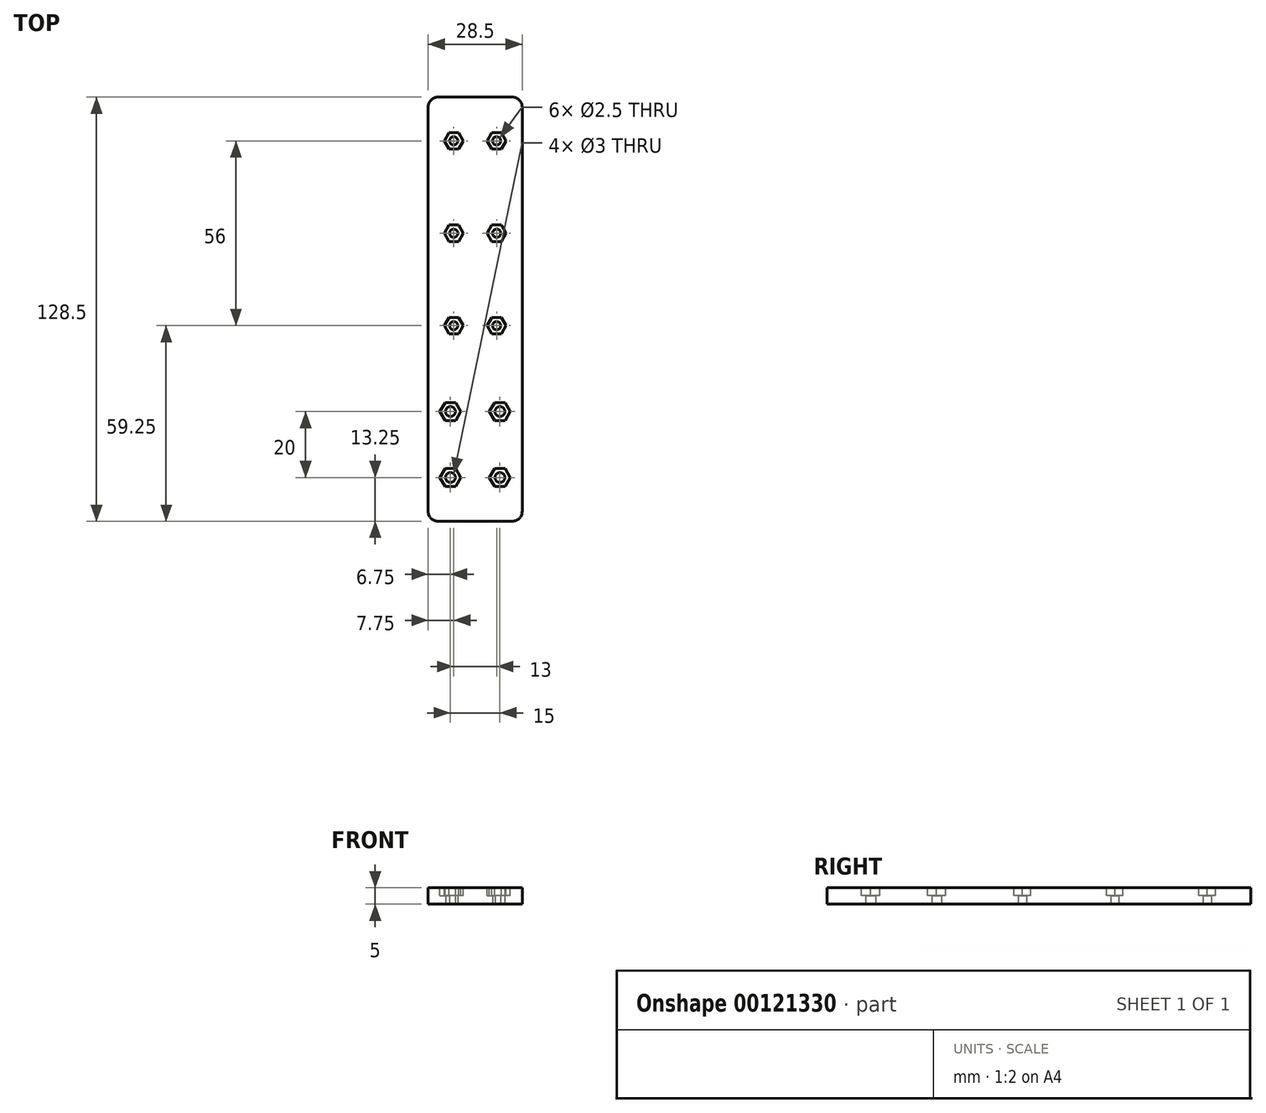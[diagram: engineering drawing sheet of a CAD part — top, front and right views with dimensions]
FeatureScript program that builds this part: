
annotation { "Feature Type Name" : "Feature", "Feature Type Description" : "" }
export const myFeature = defineFeature(function(context is Context, id is Id, definition is map)
    precondition{}
    {
        {
            var Q0;
            Q0=qCreatedBy(makeId("Top.planeOp"),FACE);
            var sketch = newSketch(context, id + "F0", { "sketchPlane" : qUnion([Q0])});
            skCircle(sketch, "E0", {"center": v(7.75, 59.25) * mm, "radius": 1.25 * mm});
            skCircle(sketch, "E1.0.1.0", {"center": v(7.75, 87.25) * mm, "radius": 1.25 * mm});
            skCircle(sketch, "E1.0.2.0", {"center": v(7.75, 115.25) * mm, "radius": 1.25 * mm});
            skCircle(sketch, "E1.1.0.0", {"center": v(20.75, 59.25) * mm, "radius": 1.25 * mm});
            skCircle(sketch, "E1.1.1.0", {"center": v(20.75, 87.25) * mm, "radius": 1.25 * mm});
            skCircle(sketch, "E1.1.2.0", {"center": v(20.75, 115.25) * mm, "radius": 1.25 * mm});
            skLineSegment(sketch, "E1.direction1", {"start": v(7.75, 59.25) * mm, "end": v(20.75, 59.25) * mm, "construction": true});
            skLineSegment(sketch, "E1.direction2", {"start": v(7.75, 59.25) * mm, "end": v(7.75, 87.25) * mm, "construction": true});
            skLineSegment(sketch, "E2.bottom", {"start": v(0, 0) * mm, "end": v(28.5, 0) * mm});
            skLineSegment(sketch, "E2.top", {"start": v(0, 128.5) * mm, "end": v(28.5, 128.5) * mm});
            skLineSegment(sketch, "E2.left", {"start": v(0, 0) * mm, "end": v(0, 128.5) * mm});
            skLineSegment(sketch, "E2.right", {"start": v(28.5, 0) * mm, "end": v(28.5, 128.5) * mm});
            skCircle(sketch, "E3", {"center": v(6.75, 13.25) * mm, "radius": 1.5 * mm});
            skCircle(sketch, "E4.0.1.0", {"center": v(6.75, 33.25) * mm, "radius": 1.5 * mm});
            skCircle(sketch, "E4.1.0.0", {"center": v(21.75, 13.25) * mm, "radius": 1.5 * mm});
            skCircle(sketch, "E4.1.1.0", {"center": v(21.75, 33.25) * mm, "radius": 1.5 * mm});
            skLineSegment(sketch, "E4.direction1", {"start": v(6.75, 13.25) * mm, "end": v(21.75, 13.25) * mm, "construction": true});
            skLineSegment(sketch, "E4.direction2", {"start": v(6.75, 13.25) * mm, "end": v(6.75, 33.25) * mm, "construction": true});
            skPoint(sketch, "E5", {"position": v(14.25, 59.25) * mm});
            skPoint(sketch, "E6", {"position": v(14.25, 13.25) * mm});
            skSolve(sketch);
        }
        {
            var Q0;
            Q0=makeQuery(id+"F0.imprint","IMPRINT",FACE,{"disambiguationData":[TD([[makeQuery(id+"F0.imprint","IMPRINT",EDGE,{"derivedFrom":sQuery(id+"F0.wireOp",EDGE,"E0")}),-1.0]])]});
            extrude(context, id + "F1", {"entities" : qUnion([Q0]), "depth" : 5 * mm});
        }
        {
            var Q0;
            Q0=makeQuery(id+"F1.opExtrude","CAP_FACE",FACE,{"disambiguationData":[OSD([sQuery(id+"F0.wireOp",EDGE,"E0"),sQuery(id+"F0.wireOp",EDGE,"E1.0.1.0"),sQuery(id+"F0.wireOp",EDGE,"E1.0.2.0"),sQuery(id+"F0.wireOp",EDGE,"E1.1.0.0"),sQuery(id+"F0.wireOp",EDGE,"E1.1.1.0"),sQuery(id+"F0.wireOp",EDGE,"E1.1.2.0"),sQuery(id+"F0.wireOp",EDGE,"E2.bottom"),sQuery(id+"F0.wireOp",EDGE,"E2.top"),sQuery(id+"F0.wireOp",EDGE,"E2.left"),sQuery(id+"F0.wireOp",EDGE,"E2.right"),sQuery(id+"F0.wireOp",EDGE,"E3"),sQuery(id+"F0.wireOp",EDGE,"E4.0.1.0"),sQuery(id+"F0.wireOp",EDGE,"E4.1.0.0"),sQuery(id+"F0.wireOp",EDGE,"E4.1.1.0")])],"isStart":false});
            var sketch = newSketch(context, id + "F2", { "sketchPlane" : qUnion([Q0])});
            skCircle(sketch, "E7.cCircle", {"center": v(21.75, 13.25) * mm, "radius": 2.75 * mm, "construction": true});
            skLineSegment(sketch, "E7.0", {"start": v(23.34, 10.5) * mm, "end": v(20.16, 10.5) * mm});
            skLineSegment(sketch, "E7.1", {"start": v(20.16, 10.5) * mm, "end": v(18.57, 13.25) * mm});
            skLineSegment(sketch, "E7.2", {"start": v(18.57, 13.25) * mm, "end": v(20.16, 16) * mm});
            skLineSegment(sketch, "E7.3", {"start": v(20.16, 16) * mm, "end": v(23.34, 16) * mm});
            skLineSegment(sketch, "E7.4", {"start": v(23.34, 16) * mm, "end": v(24.93, 13.25) * mm});
            skLineSegment(sketch, "E7.5", {"start": v(24.93, 13.25) * mm, "end": v(23.34, 10.5) * mm});
            skPoint(sketch, "E7.0.midPoint", {"position": v(21.75, 10.5) * mm});
            skCircle(sketch, "E8.cCircle", {"center": v(7.75, 59.25) * mm, "radius": 2.5 * mm, "construction": true});
            skLineSegment(sketch, "E8.0", {"start": v(9.2, 56.75) * mm, "end": v(6.3, 56.75) * mm});
            skLineSegment(sketch, "E8.1", {"start": v(6.3, 56.75) * mm, "end": v(4.86, 59.25) * mm});
            skLineSegment(sketch, "E8.2", {"start": v(4.86, 59.25) * mm, "end": v(6.3, 61.75) * mm});
            skLineSegment(sketch, "E8.3", {"start": v(6.3, 61.75) * mm, "end": v(9.2, 61.75) * mm});
            skLineSegment(sketch, "E8.4", {"start": v(9.2, 61.75) * mm, "end": v(10.64, 59.25) * mm});
            skLineSegment(sketch, "E8.5", {"start": v(10.64, 59.25) * mm, "end": v(9.2, 56.75) * mm});
            skPoint(sketch, "E8.0.midPoint", {"position": v(7.75, 56.75) * mm});
            skCircle(sketch, "E9.cCircle", {"center": v(6.75, 33.25) * mm, "radius": 2.75 * mm, "construction": true});
            skLineSegment(sketch, "E9.0", {"start": v(8.34, 30.5) * mm, "end": v(5.16, 30.5) * mm});
            skLineSegment(sketch, "E9.1", {"start": v(5.16, 30.5) * mm, "end": v(3.57, 33.25) * mm});
            skLineSegment(sketch, "E9.2", {"start": v(3.57, 33.25) * mm, "end": v(5.16, 36) * mm});
            skLineSegment(sketch, "E9.3", {"start": v(5.16, 36) * mm, "end": v(8.34, 36) * mm});
            skLineSegment(sketch, "E9.4", {"start": v(8.34, 36) * mm, "end": v(9.93, 33.25) * mm});
            skLineSegment(sketch, "E9.5", {"start": v(9.93, 33.25) * mm, "end": v(8.34, 30.5) * mm});
            skPoint(sketch, "E9.0.midPoint", {"position": v(6.75, 30.5) * mm});
            skLineSegment(sketch, "E10.0.1.0", {"start": v(9.2, 84.75) * mm, "end": v(6.3, 84.75) * mm});
            skCircle(sketch, "E10.0.1.1", {"center": v(7.75, 87.25) * mm, "radius": 2.5 * mm, "construction": true});
            skLineSegment(sketch, "E10.0.1.2", {"start": v(6.3, 84.75) * mm, "end": v(4.86, 87.25) * mm});
            skPoint(sketch, "E10.0.1.3", {"position": v(7.75, 84.75) * mm});
            skLineSegment(sketch, "E10.0.1.4", {"start": v(4.86, 87.25) * mm, "end": v(6.3, 89.75) * mm});
            skLineSegment(sketch, "E10.0.1.5", {"start": v(10.64, 87.25) * mm, "end": v(9.2, 84.75) * mm});
            skLineSegment(sketch, "E10.0.1.6", {"start": v(6.3, 89.75) * mm, "end": v(9.2, 89.75) * mm});
            skLineSegment(sketch, "E10.0.1.7", {"start": v(9.2, 89.75) * mm, "end": v(10.64, 87.25) * mm});
            skLineSegment(sketch, "E10.0.2.0", {"start": v(9.2, 112.75) * mm, "end": v(6.3, 112.75) * mm});
            skCircle(sketch, "E10.0.2.1", {"center": v(7.75, 115.25) * mm, "radius": 2.5 * mm, "construction": true});
            skLineSegment(sketch, "E10.0.2.2", {"start": v(6.3, 112.75) * mm, "end": v(4.86, 115.25) * mm});
            skPoint(sketch, "E10.0.2.3", {"position": v(7.75, 112.75) * mm});
            skLineSegment(sketch, "E10.0.2.4", {"start": v(4.86, 115.25) * mm, "end": v(6.3, 117.75) * mm});
            skLineSegment(sketch, "E10.0.2.5", {"start": v(10.64, 115.25) * mm, "end": v(9.2, 112.75) * mm});
            skLineSegment(sketch, "E10.0.2.6", {"start": v(6.3, 117.75) * mm, "end": v(9.2, 117.75) * mm});
            skLineSegment(sketch, "E10.0.2.7", {"start": v(9.2, 117.75) * mm, "end": v(10.64, 115.25) * mm});
            skLineSegment(sketch, "E10.1.0.0", {"start": v(22.2, 56.75) * mm, "end": v(19.3, 56.75) * mm});
            skCircle(sketch, "E10.1.0.1", {"center": v(20.75, 59.25) * mm, "radius": 2.5 * mm, "construction": true});
            skLineSegment(sketch, "E10.1.0.2", {"start": v(19.3, 56.75) * mm, "end": v(17.86, 59.25) * mm});
            skPoint(sketch, "E10.1.0.3", {"position": v(20.75, 56.75) * mm});
            skLineSegment(sketch, "E10.1.0.4", {"start": v(17.86, 59.25) * mm, "end": v(19.3, 61.75) * mm});
            skLineSegment(sketch, "E10.1.0.5", {"start": v(23.64, 59.25) * mm, "end": v(22.2, 56.75) * mm});
            skLineSegment(sketch, "E10.1.0.6", {"start": v(19.3, 61.75) * mm, "end": v(22.2, 61.75) * mm});
            skLineSegment(sketch, "E10.1.0.7", {"start": v(22.2, 61.75) * mm, "end": v(23.64, 59.25) * mm});
            skLineSegment(sketch, "E10.1.1.0", {"start": v(22.2, 84.75) * mm, "end": v(19.3, 84.75) * mm});
            skCircle(sketch, "E10.1.1.1", {"center": v(20.75, 87.25) * mm, "radius": 2.5 * mm, "construction": true});
            skLineSegment(sketch, "E10.1.1.2", {"start": v(19.3, 84.75) * mm, "end": v(17.86, 87.25) * mm});
            skPoint(sketch, "E10.1.1.3", {"position": v(20.75, 84.75) * mm});
            skLineSegment(sketch, "E10.1.1.4", {"start": v(17.86, 87.25) * mm, "end": v(19.3, 89.75) * mm});
            skLineSegment(sketch, "E10.1.1.5", {"start": v(23.64, 87.25) * mm, "end": v(22.2, 84.75) * mm});
            skLineSegment(sketch, "E10.1.1.6", {"start": v(19.3, 89.75) * mm, "end": v(22.2, 89.75) * mm});
            skLineSegment(sketch, "E10.1.1.7", {"start": v(22.2, 89.75) * mm, "end": v(23.64, 87.25) * mm});
            skLineSegment(sketch, "E10.1.2.0", {"start": v(22.2, 112.75) * mm, "end": v(19.3, 112.75) * mm});
            skCircle(sketch, "E10.1.2.1", {"center": v(20.75, 115.25) * mm, "radius": 2.5 * mm, "construction": true});
            skLineSegment(sketch, "E10.1.2.2", {"start": v(19.3, 112.75) * mm, "end": v(17.86, 115.25) * mm});
            skPoint(sketch, "E10.1.2.3", {"position": v(20.75, 112.75) * mm});
            skLineSegment(sketch, "E10.1.2.4", {"start": v(17.86, 115.25) * mm, "end": v(19.3, 117.75) * mm});
            skLineSegment(sketch, "E10.1.2.5", {"start": v(23.64, 115.25) * mm, "end": v(22.2, 112.75) * mm});
            skLineSegment(sketch, "E10.1.2.6", {"start": v(19.3, 117.75) * mm, "end": v(22.2, 117.75) * mm});
            skLineSegment(sketch, "E10.1.2.7", {"start": v(22.2, 117.75) * mm, "end": v(23.64, 115.25) * mm});
            skLineSegment(sketch, "E10.direction1", {"start": v(6.3, 56.75) * mm, "end": v(19.3, 56.75) * mm, "construction": true});
            skLineSegment(sketch, "E10.direction2", {"start": v(6.3, 56.75) * mm, "end": v(6.3, 84.75) * mm, "construction": true});
            skCircle(sketch, "E11.cCircle", {"center": v(6.75, 13.25) * mm, "radius": 2.75 * mm, "construction": true});
            skLineSegment(sketch, "E11.0", {"start": v(8.34, 10.5) * mm, "end": v(5.16, 10.5) * mm});
            skLineSegment(sketch, "E11.1", {"start": v(5.16, 10.5) * mm, "end": v(3.57, 13.25) * mm});
            skLineSegment(sketch, "E11.2", {"start": v(3.57, 13.25) * mm, "end": v(5.16, 16) * mm});
            skLineSegment(sketch, "E11.3", {"start": v(5.16, 16) * mm, "end": v(8.34, 16) * mm});
            skLineSegment(sketch, "E11.4", {"start": v(8.34, 16) * mm, "end": v(9.93, 13.25) * mm});
            skLineSegment(sketch, "E11.5", {"start": v(9.93, 13.25) * mm, "end": v(8.34, 10.5) * mm});
            skPoint(sketch, "E11.0.midPoint", {"position": v(6.75, 10.5) * mm});
            skCircle(sketch, "E12.cCircle", {"center": v(21.75, 33.25) * mm, "radius": 2.75 * mm, "construction": true});
            skLineSegment(sketch, "E12.0", {"start": v(23.34, 30.5) * mm, "end": v(20.16, 30.5) * mm});
            skLineSegment(sketch, "E12.1", {"start": v(20.16, 30.5) * mm, "end": v(18.57, 33.25) * mm});
            skLineSegment(sketch, "E12.2", {"start": v(18.57, 33.25) * mm, "end": v(20.16, 36) * mm});
            skLineSegment(sketch, "E12.3", {"start": v(20.16, 36) * mm, "end": v(23.34, 36) * mm});
            skLineSegment(sketch, "E12.4", {"start": v(23.34, 36) * mm, "end": v(24.93, 33.25) * mm});
            skLineSegment(sketch, "E12.5", {"start": v(24.93, 33.25) * mm, "end": v(23.34, 30.5) * mm});
            skPoint(sketch, "E12.0.midPoint", {"position": v(21.75, 30.5) * mm});
            skSolve(sketch);
        }
        {
            var Q0;
            Q0=makeQuery(id+"F2.imprint","IMPRINT",FACE,{"disambiguationData":[TD([[makeQuery(id+"F2.imprint","IMPRINT",EDGE,{"derivedFrom":sQuery(id+"F2.wireOp",EDGE,"E10.0.1.0")}),-1.0]])]});
            var Q1;
            Q1=makeQuery(id+"F2.imprint","IMPRINT",FACE,{"disambiguationData":[TD([[makeQuery(id+"F2.imprint","IMPRINT",EDGE,{"derivedFrom":sQuery(id+"F2.wireOp",EDGE,"E10.1.1.0")}),-1.0]])]});
            var Q2;
            Q2=makeQuery(id+"F2.imprint","IMPRINT",FACE,{"disambiguationData":[TD([[makeQuery(id+"F2.imprint","IMPRINT",EDGE,{"derivedFrom":sQuery(id+"F2.wireOp",EDGE,"E10.0.2.0")}),-1.0]])]});
            var Q3;
            Q3=makeQuery(id+"F2.imprint","IMPRINT",FACE,{"disambiguationData":[TD([[makeQuery(id+"F2.imprint","IMPRINT",EDGE,{"derivedFrom":sQuery(id+"F2.wireOp",EDGE,"E10.1.2.0")}),-1.0]])]});
            var Q4;
            Q4=makeQuery(id+"F2.imprint","IMPRINT",FACE,{"disambiguationData":[TD([[makeQuery(id+"F2.imprint","IMPRINT",EDGE,{"derivedFrom":sQuery(id+"F2.wireOp",EDGE,"E10.1.0.0")}),-1.0]])]});
            var Q5;
            Q5=makeQuery(id+"F2.imprint","IMPRINT",FACE,{"disambiguationData":[TD([[makeQuery(id+"F2.imprint","IMPRINT",EDGE,{"derivedFrom":sQuery(id+"F2.wireOp",EDGE,"E8.0")}),-1.0]])]});
            var Q6;
            Q6=makeQuery(id+"F2.imprint","IMPRINT",FACE,{"disambiguationData":[TD([[makeQuery(id+"F2.imprint","IMPRINT",EDGE,{"derivedFrom":sQuery(id+"F2.wireOp",EDGE,"E9.0")}),-1.0]])]});
            var Q7;
            Q7=makeQuery(id+"F2.imprint","IMPRINT",FACE,{"disambiguationData":[TD([[makeQuery(id+"F2.imprint","IMPRINT",EDGE,{"derivedFrom":sQuery(id+"F2.wireOp",EDGE,"E7.0")}),-1.0]])]});
            var Q8;
            Q8=makeQuery(id+"F2.imprint","IMPRINT",FACE,{"disambiguationData":[TD([[makeQuery(id+"F2.imprint","IMPRINT",EDGE,{"derivedFrom":sQuery(id+"F2.wireOp",EDGE,"E11.0")}),-1.0]])]});
            var Q9;
            Q9=makeQuery(id+"F2.imprint","IMPRINT",FACE,{"disambiguationData":[TD([[makeQuery(id+"F2.imprint","IMPRINT",EDGE,{"derivedFrom":sQuery(id+"F2.wireOp",EDGE,"E12.0")}),-1.0]])]});
            extrude(context, id + "F3", {"entities" : qUnion([Q0, Q1, Q2, Q3, Q4, Q5, Q6, Q7, Q8, Q9]), "operationType" : NewBodyOperationType.REMOVE, "oppositeDirection" : true, "depth" : 2.4 * mm});
        }
        {
            var Q0;
            Q0=makeQuery(id+"F1.opExtrude","SWEPT_EDGE",EDGE,{"disambiguationData":[OSD([sQuery(id+"F0.wireOp",EDGE,"E2.bottom"),sQuery(id+"F0.wireOp",EDGE,"E2.left")])]});
            var Q1;
            Q1=makeQuery(id+"F1.opExtrude","SWEPT_EDGE",EDGE,{"disambiguationData":[OSD([sQuery(id+"F0.wireOp",EDGE,"E2.bottom"),sQuery(id+"F0.wireOp",EDGE,"E2.right")])]});
            var Q2;
            Q2=makeQuery(id+"F1.opExtrude","SWEPT_EDGE",EDGE,{"disambiguationData":[OSD([sQuery(id+"F0.wireOp",EDGE,"E2.top"),sQuery(id+"F0.wireOp",EDGE,"E2.left")])]});
            var Q3;
            Q3=makeQuery(id+"F1.opExtrude","SWEPT_EDGE",EDGE,{"disambiguationData":[OSD([sQuery(id+"F0.wireOp",EDGE,"E2.top"),sQuery(id+"F0.wireOp",EDGE,"E2.right")])]});
            fillet(context, id + "F4", {"entities" : qUnion([Q0, Q1, Q2, Q3]), "radius" : 3 * mm, "tangentPropagation" : true, "allowEdgeOverflow" : false});
        }
    });
